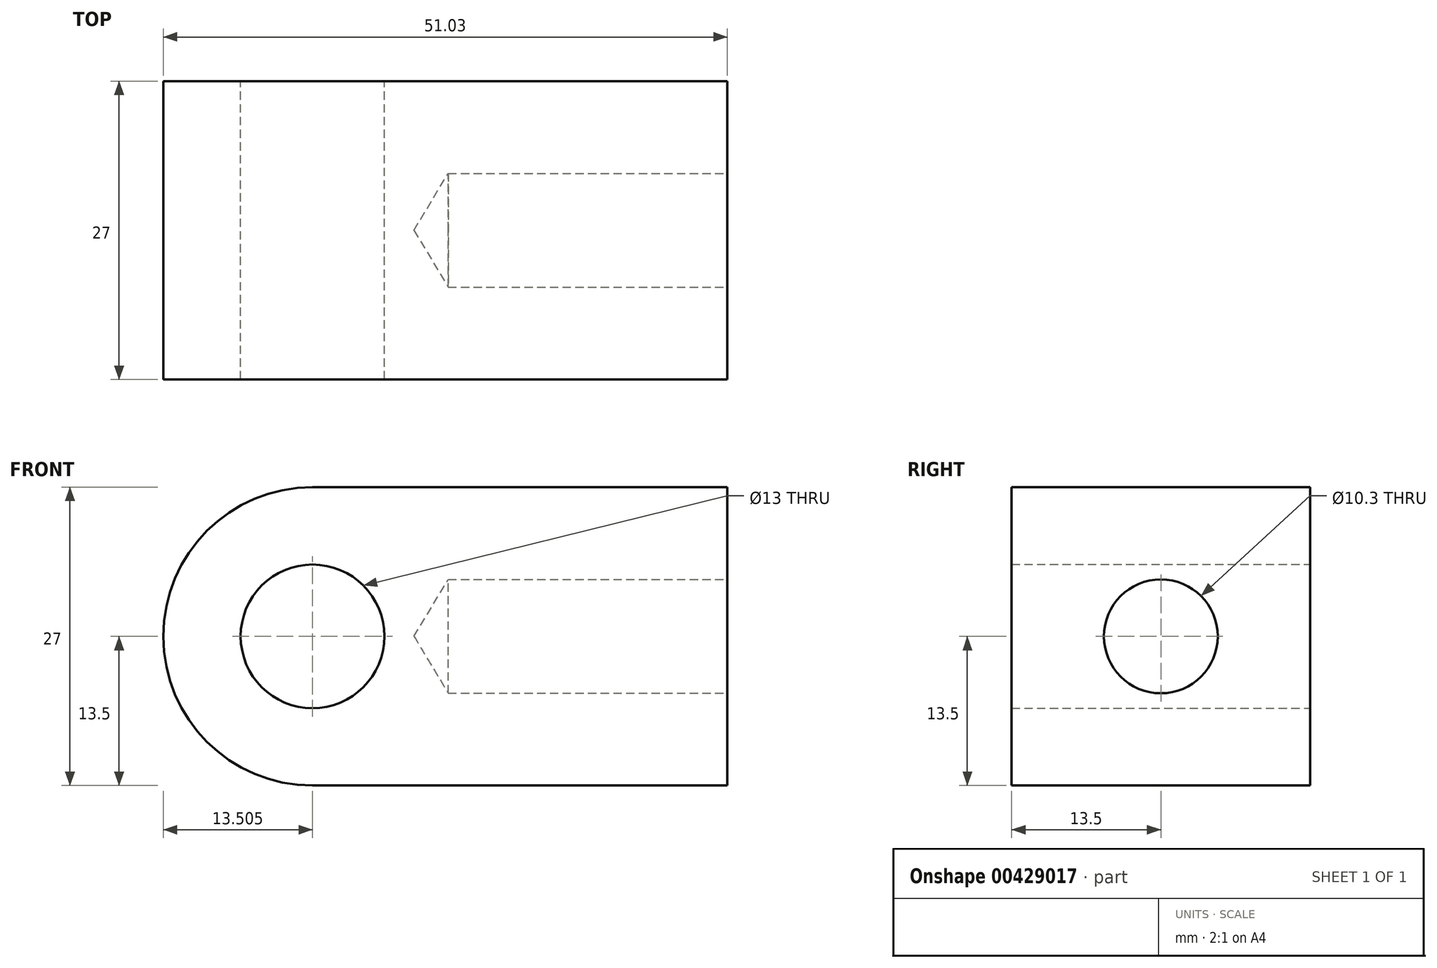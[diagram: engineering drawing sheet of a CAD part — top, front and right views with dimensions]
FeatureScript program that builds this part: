
annotation { "Feature Type Name" : "Feature", "Feature Type Description" : "" }
export const myFeature = defineFeature(function(context is Context, id is Id, definition is map)
    precondition{}
    {
        {
            var Q0;
            Q0=qCreatedBy(makeId("Front.planeOp"),FACE);
            var sketch = newSketch(context, id + "F0", { "sketchPlane" : qUnion([Q0])});
            skCircle(sketch, "E0", {"center": v(-37.53, 0) * mm, "radius": 6.5 * mm});
            skCircle(sketch, "E1", {"center": v(-37.53, 0) * mm, "radius": 13.5 * mm});
            skLineSegment(sketch, "E2", {"start": v(-37.53, -13.5) * mm, "end": v(0, -13.5) * mm});
            skLineSegment(sketch, "E3", {"start": v(-37.53, 13.5) * mm, "end": v(0, 13.5) * mm});
            skLineSegment(sketch, "E4", {"start": v(0, 13.5) * mm, "end": v(0, -13.5) * mm});
            skSolve(sketch);
        }
        {
            var Q0;
            Q0 = qSketchRegion(id + "F0", true);
            extrude(context, id + "F1", {"entities" : qUnion([Q0]), "endBound" : BoundingType.SYMMETRIC, "depth" : 27 * mm});
        }
        {
            var Q0;
            Q0=qCreatedBy(makeId("Right.planeOp"),FACE);
            var sketch = newSketch(context, id + "F2", { "sketchPlane" : qUnion([Q0])});
            skPoint(sketch, "E5", {"position": v(0, 0) * mm});
            skSolve(sketch);
        }
        {
            var Q0;
            Q0=sQuery(id+"F2.wireOp",VERTEX,"E5");
            var Q1;
            Q1=makeQuery(id+"F1.opExtrude","SWEPT_BODY",BODY,{"disambiguationData":[OSD([sQuery(id+"F0.wireOp",EDGE,"E0"),sQuery(id+"F0.wireOp",EDGE,"E1"),sQuery(id+"F0.wireOp",EDGE,"E2"),sQuery(id+"F0.wireOp",EDGE,"E3"),sQuery(id+"F0.wireOp",EDGE,"E4")])]});
            hole(context, id + "F3", {"style" : HoleStyle.SIMPLE, "endStyle" : HoleEndStyle.BLIND, "standardTappedOrClearance" : lookupTablePath({ "standard" : "ISO", "engagement" : "75%", "pitch" : "1.75 mm", "size" : "M12", "type" : "Tapped" }), "standardBlindInLast" : lookupTablePath({ "standard" : "ISO", "engagement" : "75%", "pitch" : "1.75 mm", "size" : "M12", "type" : "Tapped" }), "holeDiameter" : 10.3 * mm, "showTappedDepth" : true, "holeDepth" : 25.25 * mm, "isTappedThrough" : true, "tappedDepth" : 20 * mm, "tapClearance" : 3, "startFromSketch" : true, "locations" : qUnion([Q0]), "scope" : qUnion([Q1]), "majorDiameter" : 12 * mm});
        }
    });
